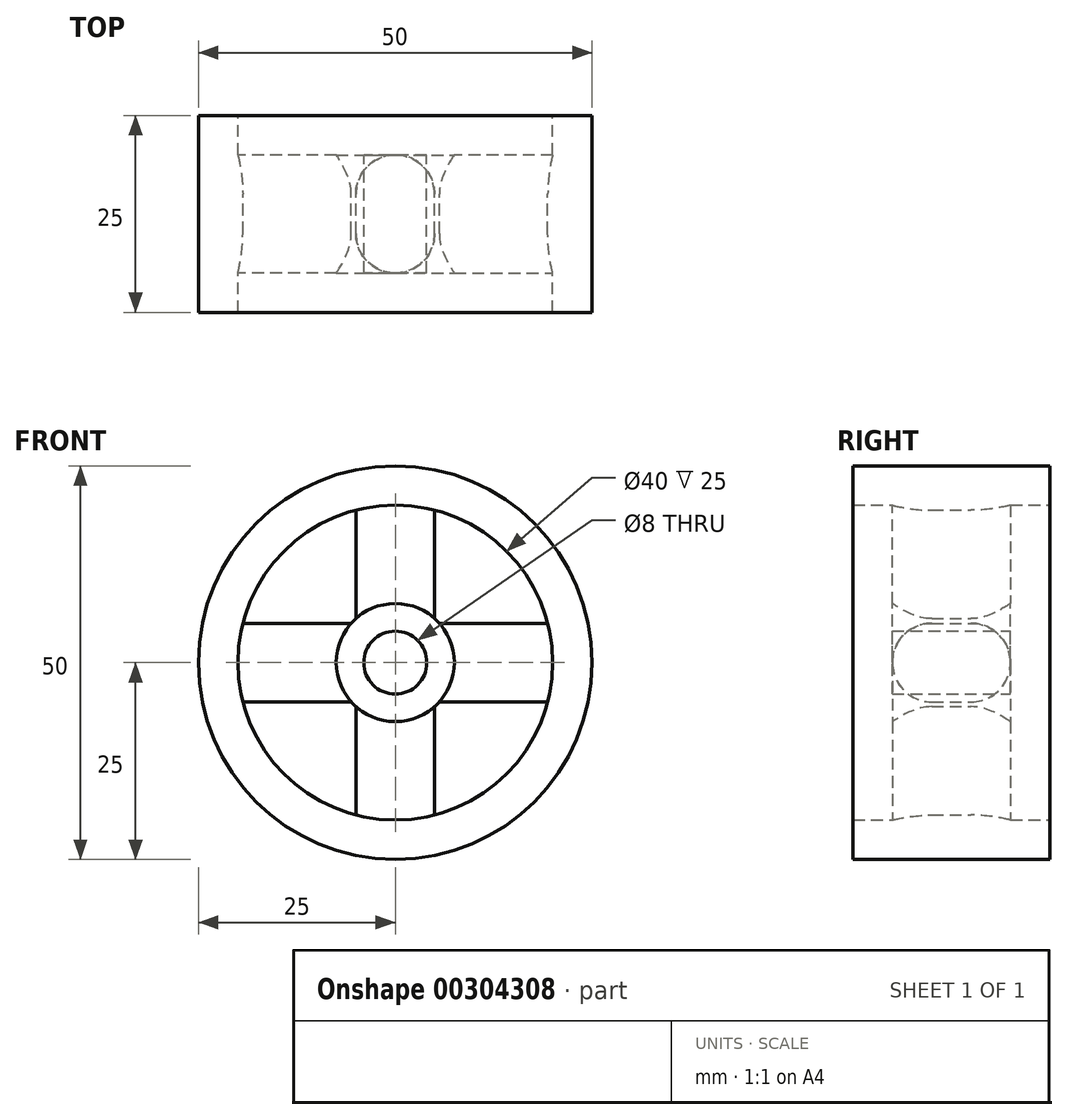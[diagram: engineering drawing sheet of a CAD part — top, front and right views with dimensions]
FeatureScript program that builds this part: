
annotation { "Feature Type Name" : "Feature", "Feature Type Description" : "" }
export const myFeature = defineFeature(function(context is Context, id is Id, definition is map)
    precondition{}
    {
        {
            var Q0;
            Q0=qCreatedBy(makeId("Front.planeOp"),FACE);
            var sketch = newSketch(context, id + "F0", { "sketchPlane" : qUnion([Q0])});
            skCircle(sketch, "E0", {"center": v(0, 0) * mm, "radius": 25 * mm});
            skArc(sketch, "E1", {"start": v(-5.6, -5) * mm, "mid": v(-5.3, -5.3) * mm, "end": v(-5, -5.6) * mm});
            skCircle(sketch, "E2", {"center": v(0, 0) * mm, "radius": 4 * mm});
            skLineSegment(sketch, "E3", {"start": v(0, 0) * mm, "end": v(0, 20) * mm, "construction": true});
            skLineSegment(sketch, "E4.0", {"start": v(5, 5.6) * mm, "end": v(5, 19.36) * mm});
            skLineSegment(sketch, "E5.0", {"start": v(-5, 5.6) * mm, "end": v(-5, 19.36) * mm});
            skLineSegment(sketch, "E6", {"start": v(0, 0) * mm, "end": v(0, -20) * mm, "construction": true});
            skLineSegment(sketch, "E7", {"start": v(0, 0) * mm, "end": v(20, 0) * mm, "construction": true});
            skLineSegment(sketch, "E8", {"start": v(0, 0) * mm, "end": v(-20, 0) * mm, "construction": true});
            skLineSegment(sketch, "E9.0", {"start": v(5, -5.6) * mm, "end": v(5, -19.36) * mm});
            skLineSegment(sketch, "E10.0", {"start": v(-5, -5.6) * mm, "end": v(-5, -19.36) * mm});
            skLineSegment(sketch, "E11.0", {"start": v(-5.6, 5) * mm, "end": v(-19.36, 5) * mm});
            skLineSegment(sketch, "E12.0", {"start": v(-5.6, -5) * mm, "end": v(-19.36, -5) * mm});
            skLineSegment(sketch, "E13.0", {"start": v(5.6, -5) * mm, "end": v(19.36, -5) * mm});
            skLineSegment(sketch, "E14.0", {"start": v(5.6, 5) * mm, "end": v(19.36, 5) * mm});
            skLineSegment(sketch, "E15.trimOffspring", {"start": v(-5, 24.5) * mm, "end": v(-5, 25) * mm});
            skLineSegment(sketch, "E16.trimOffspring", {"start": v(5, 24.5) * mm, "end": v(5, 25) * mm});
            skLineSegment(sketch, "E17.trimOffspring", {"start": v(-24.5, 5) * mm, "end": v(-25, 5) * mm});
            skLineSegment(sketch, "E18.trimOffspring", {"start": v(-24.5, -5) * mm, "end": v(-25, -5) * mm});
            skArc(sketch, "E19.trimOffspring", {"start": v(5, -5.6) * mm, "mid": v(5.3, -5.3) * mm, "end": v(5.6, -5) * mm});
            skLineSegment(sketch, "E20.trimOffspring", {"start": v(-5, -24.5) * mm, "end": v(-5, -25) * mm});
            skLineSegment(sketch, "E21.trimOffspring", {"start": v(5, -24.5) * mm, "end": v(5, -25) * mm});
            skLineSegment(sketch, "E22.trimOffspring", {"start": v(24.5, -5) * mm, "end": v(25, -5) * mm});
            skLineSegment(sketch, "E23.trimOffspring", {"start": v(24.5, 5) * mm, "end": v(25, 5) * mm});
            skArc(sketch, "E24.trimOffspring", {"start": v(5.6, 5) * mm, "mid": v(5.3, 5.3) * mm, "end": v(5, 5.6) * mm});
            skArc(sketch, "E25.trimOffspring", {"start": v(-5, 5.6) * mm, "mid": v(-5.3, 5.3) * mm, "end": v(-5.6, 5) * mm});
            skCircle(sketch, "E26", {"center": v(0, 0) * mm, "radius": 20 * mm});
            skPoint(sketch, "E27", {"position": v(-5.3, 5.3) * mm});
            skSolve(sketch);
        }
        {
            var Q0;
            {var subQ3=sQuery(id+"F0.wireOp",EDGE,"E0");var subQ12=makeQuery(id+"F0.imprint","IMPRINT",VERTEX,{"disambiguationData":[OD(1.0)],"derivedFrom":subQ3});Q0=makeQuery(id+"F0.imprint","IMPRINT",FACE,{"disambiguationData":[TD([[makeQuery(id+"F0.imprint","IMPRINT",EDGE,{"disambiguationData":[TD([[subQ12,1.0]])],"derivedFrom":subQ3}),1.0]])]});}
            extrude(context, id + "F1", {"entities" : qUnion([Q0]), "endBound" : BoundingType.SYMMETRIC, "depth" : 25 * mm});
        }
        {
            var Q0;
            Q0=makeQuery(id+"F0.imprint","IMPRINT",FACE,{"disambiguationData":[TD([[makeQuery(id+"F0.imprint","IMPRINT",EDGE,{"derivedFrom":sQuery(id+"F0.wireOp",EDGE,"E1")}),1.0]])]});
            extrude(context, id + "F2", {"entities" : qUnion([Q0]), "operationType" : NewBodyOperationType.ADD, "endBound" : BoundingType.SYMMETRIC, "depth" : 15 * mm});
        }
        {
            var Q0;
            Q0=makeQuery(id+"F2.opExtrude","CAP_EDGE",EDGE,{"disambiguationData":[OSD([sQuery(id+"F0.wireOp",EDGE,"E14.0")])],"isStart":true});
            fillet(context, id + "F3", {"entities" : qUnion([Q0]), "radius" : 5 * mm, "tangentPropagation" : true, "allowEdgeOverflow" : false});
        }
        {
            var Q0;
            Q0=makeQuery(id+"F2.opExtrude","CAP_EDGE",EDGE,{"disambiguationData":[OSD([sQuery(id+"F0.wireOp",EDGE,"E13.0")])],"isStart":true});
            var Q1;
            Q1=makeQuery(id+"F2.opExtrude","CAP_EDGE",EDGE,{"disambiguationData":[OSD([sQuery(id+"F0.wireOp",EDGE,"E11.0")])],"isStart":true});
            var Q2;
            Q2=makeQuery(id+"F2.opExtrude","CAP_EDGE",EDGE,{"disambiguationData":[OSD([sQuery(id+"F0.wireOp",EDGE,"E12.0")])],"isStart":true});
            var Q3;
            Q3=makeQuery(id+"F2.opExtrude","CAP_EDGE",EDGE,{"disambiguationData":[OSD([sQuery(id+"F0.wireOp",EDGE,"E10.0")])],"isStart":true});
            var Q4;
            Q4=makeQuery(id+"F2.opExtrude","CAP_EDGE",EDGE,{"disambiguationData":[OSD([sQuery(id+"F0.wireOp",EDGE,"E9.0")])],"isStart":true});
            var Q5;
            Q5=makeQuery(id+"F2.opExtrude","CAP_EDGE",EDGE,{"disambiguationData":[OSD([sQuery(id+"F0.wireOp",EDGE,"E5.0")])],"isStart":true});
            var Q6;
            Q6=makeQuery(id+"F2.opExtrude","CAP_EDGE",EDGE,{"disambiguationData":[OSD([sQuery(id+"F0.wireOp",EDGE,"E4.0")])],"isStart":true});
            var Q7;
            Q7=makeQuery(id+"F2.opExtrude","CAP_EDGE",EDGE,{"disambiguationData":[OSD([sQuery(id+"F0.wireOp",EDGE,"E14.0")])],"isStart":false});
            var Q8;
            Q8=makeQuery(id+"F2.opExtrude","CAP_EDGE",EDGE,{"disambiguationData":[OSD([sQuery(id+"F0.wireOp",EDGE,"E13.0")])],"isStart":false});
            var Q9;
            Q9=makeQuery(id+"F2.opExtrude","CAP_EDGE",EDGE,{"disambiguationData":[OSD([sQuery(id+"F0.wireOp",EDGE,"E9.0")])],"isStart":false});
            var Q10;
            Q10=makeQuery(id+"F2.opExtrude","CAP_EDGE",EDGE,{"disambiguationData":[OSD([sQuery(id+"F0.wireOp",EDGE,"E10.0")])],"isStart":false});
            var Q11;
            Q11=makeQuery(id+"F2.opExtrude","CAP_EDGE",EDGE,{"disambiguationData":[OSD([sQuery(id+"F0.wireOp",EDGE,"E12.0")])],"isStart":false});
            var Q12;
            Q12=makeQuery(id+"F2.opExtrude","CAP_EDGE",EDGE,{"disambiguationData":[OSD([sQuery(id+"F0.wireOp",EDGE,"E11.0")])],"isStart":false});
            var Q13;
            Q13=makeQuery(id+"F2.opExtrude","CAP_EDGE",EDGE,{"disambiguationData":[OSD([sQuery(id+"F0.wireOp",EDGE,"E5.0")])],"isStart":false});
            var Q14;
            Q14=makeQuery(id+"F2.opExtrude","CAP_EDGE",EDGE,{"disambiguationData":[OSD([sQuery(id+"F0.wireOp",EDGE,"E4.0")])],"isStart":false});
            fillet(context, id + "F4", {"entities" : qUnion([Q0, Q1, Q2, Q3, Q4, Q5, Q6, Q7, Q8, Q9, Q10, Q11, Q12, Q13, Q14]), "radius" : 5 * mm, "tangentPropagation" : true, "allowEdgeOverflow" : false});
        }
    });
